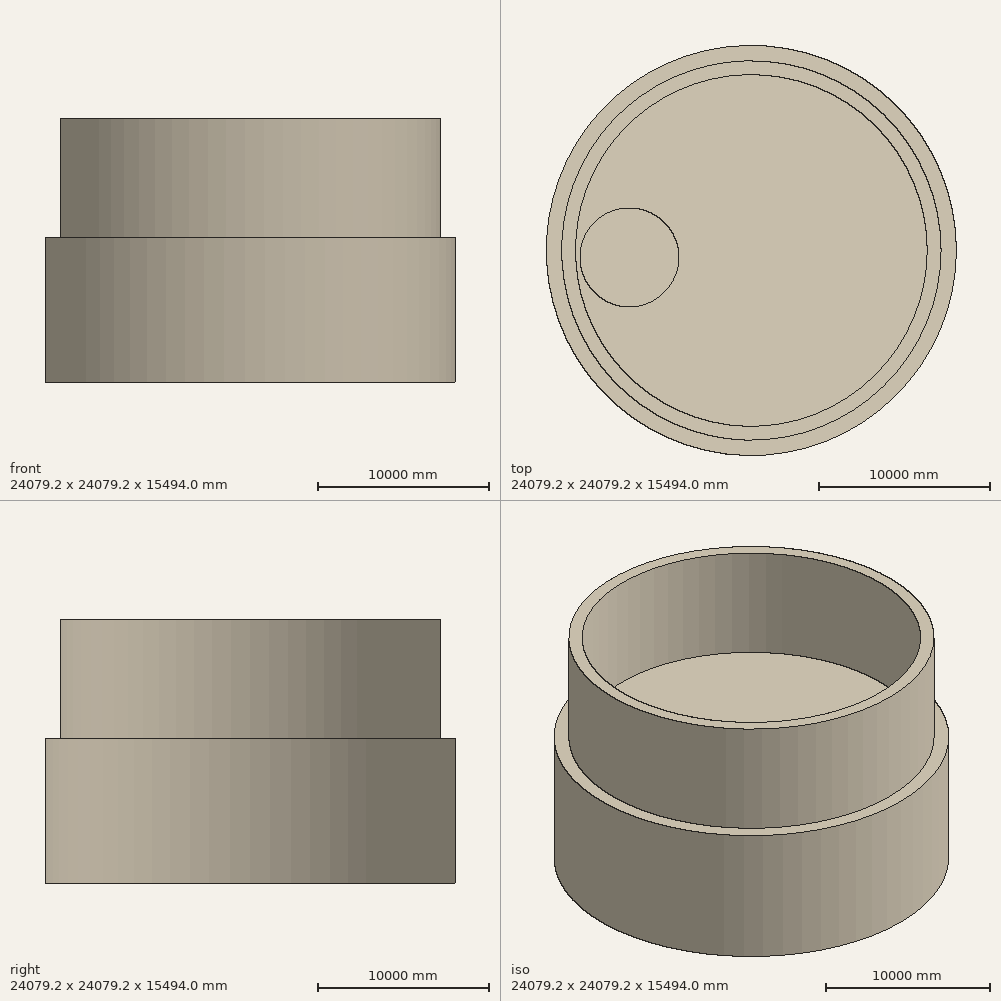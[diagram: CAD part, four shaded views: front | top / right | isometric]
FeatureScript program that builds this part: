
annotation { "Feature Type Name" : "Feature", "Feature Type Description" : "" }
export const myFeature = defineFeature(function(context is Context, id is Id, definition is map)
    precondition{}
    {
        {
            var Q0;
            Q0=qCreatedBy(makeId("Top.planeOp"),FACE);
            var sketch = newSketch(context, id + "F0", { "sketchPlane" : qUnion([Q0])});
            skCircle(sketch, "E0", {"center": v(0, 0) * mm, "radius": 12039.6 * mm});
            skSolve(sketch);
        }
        {
            var Q0;
            Q0=makeQuery(id+"F0.imprint","IMPRINT",FACE,{"disambiguationData":[TD([[makeQuery(id+"F0.imprint","IMPRINT",EDGE,{"derivedFrom":sQuery(id+"F0.wireOp",EDGE,"E0")}),1.0]])]});
            extrude(context, id + "F1", {"entities" : qUnion([Q0]), "oppositeDirection" : true, "depth" : 762 * mm, "offsetDistance" : 25.4 * mm});
        }
        {
            var Q0;
            Q0=makeQuery(id+"F1.opExtrude","CAP_FACE",FACE,{"disambiguationData":[OSD([sQuery(id+"F0.wireOp",EDGE,"E0")])],"isStart":true});
            var sketch = newSketch(context, id + "F2", { "sketchPlane" : qUnion([Q0])});
            skCircle(sketch, "E1.0", {"center": v(0, 0) * mm, "radius": 11226.8 * mm});
            skCircle(sketch, "E2.0", {"center": v(0, 0) * mm, "radius": 12045.95 * mm});
            skSolve(sketch);
        }
        {
            var Q0;
            Q0=makeQuery(id+"F2.imprint","IMPRINT",FACE,{"disambiguationData":[TD([[makeQuery(id+"F2.imprint","IMPRINT",EDGE,{"derivedFrom":sQuery(id+"F2.wireOp",EDGE,"E1.0")}),-1.0]])]});
            extrude(context, id + "F3", {"entities" : qUnion([Q0]), "operationType" : NewBodyOperationType.ADD, "depth" : 6985 * mm, "offsetDistance" : 25.4 * mm});
        }
        {
            var Q0;
            Q0=makeQuery(id+"F3.opExtrude","CAP_FACE",FACE,{"disambiguationData":[OSD([sQuery(id+"F0.wireOp",EDGE,"E0"),sQuery(id+"F2.wireOp",EDGE,"E1.0")])],"isStart":false});
            var sketch = newSketch(context, id + "F4", { "sketchPlane" : qUnion([Q0])});
            skCircle(sketch, "E3", {"center": v(0, 0) * mm, "radius": 12039.6 * mm});
            skSolve(sketch);
        }
        {
            var Q0;
            Q0 = qSketchRegion(id + "F4", true);
            extrude(context, id + "F5", {"entities" : qUnion([Q0]), "operationType" : NewBodyOperationType.ADD, "depth" : 762 * mm, "offsetDistance" : 25.4 * mm});
        }
        {
            var Q0;
            Q0=makeQuery(id+"F5.opExtrude","CAP_FACE",FACE,{"disambiguationData":[OSD([sQuery(id+"F4.wireOp",EDGE,"E3")])],"isStart":false});
            var sketch = newSketch(context, id + "F6", { "sketchPlane" : qUnion([Q0])});
            skCircle(sketch, "E4", {"center": v(-7156.66, -411.35) * mm, "radius": 2906.5 * mm});
            skSolve(sketch);
        }
        {
            var Q0;
            Q0 = qSketchRegion(id + "F6", true);
            extrude(context, id + "F7", {"entities" : qUnion([Q0]), "operationType" : NewBodyOperationType.REMOVE, "oppositeDirection" : true, "depth" : 762 * mm, "offsetDistance" : 25.4 * mm});
        }
        {
            var Q0;
            Q0=makeQuery(id+"F5.opExtrude","CAP_FACE",FACE,{"disambiguationData":[OSD([sQuery(id+"F4.wireOp",EDGE,"E3")])],"isStart":false});
            var sketch = newSketch(context, id + "F8", { "sketchPlane" : qUnion([Q0])});
            skCircle(sketch, "E5", {"center": v(0, 0) * mm, "radius": 11137.9 * mm});
            skCircle(sketch, "E6.0", {"center": v(0, 0) * mm, "radius": 10325.1 * mm});
            skCircle(sketch, "E7.0", {"center": v(0, 0) * mm, "radius": 12045.95 * mm});
            skSolve(sketch);
        }
        {
            var Q0;
            Q0=makeQuery(id+"F8.imprint","IMPRINT",FACE,{"disambiguationData":[TD([[makeQuery(id+"F8.imprint","IMPRINT",EDGE,{"derivedFrom":sQuery(id+"F8.wireOp",EDGE,"E5")}),1.0]])]});
            extrude(context, id + "F9", {"entities" : qUnion([Q0]), "operationType" : NewBodyOperationType.ADD, "depth" : 6985 * mm, "offsetDistance" : 25.4 * mm});
        }
    });
